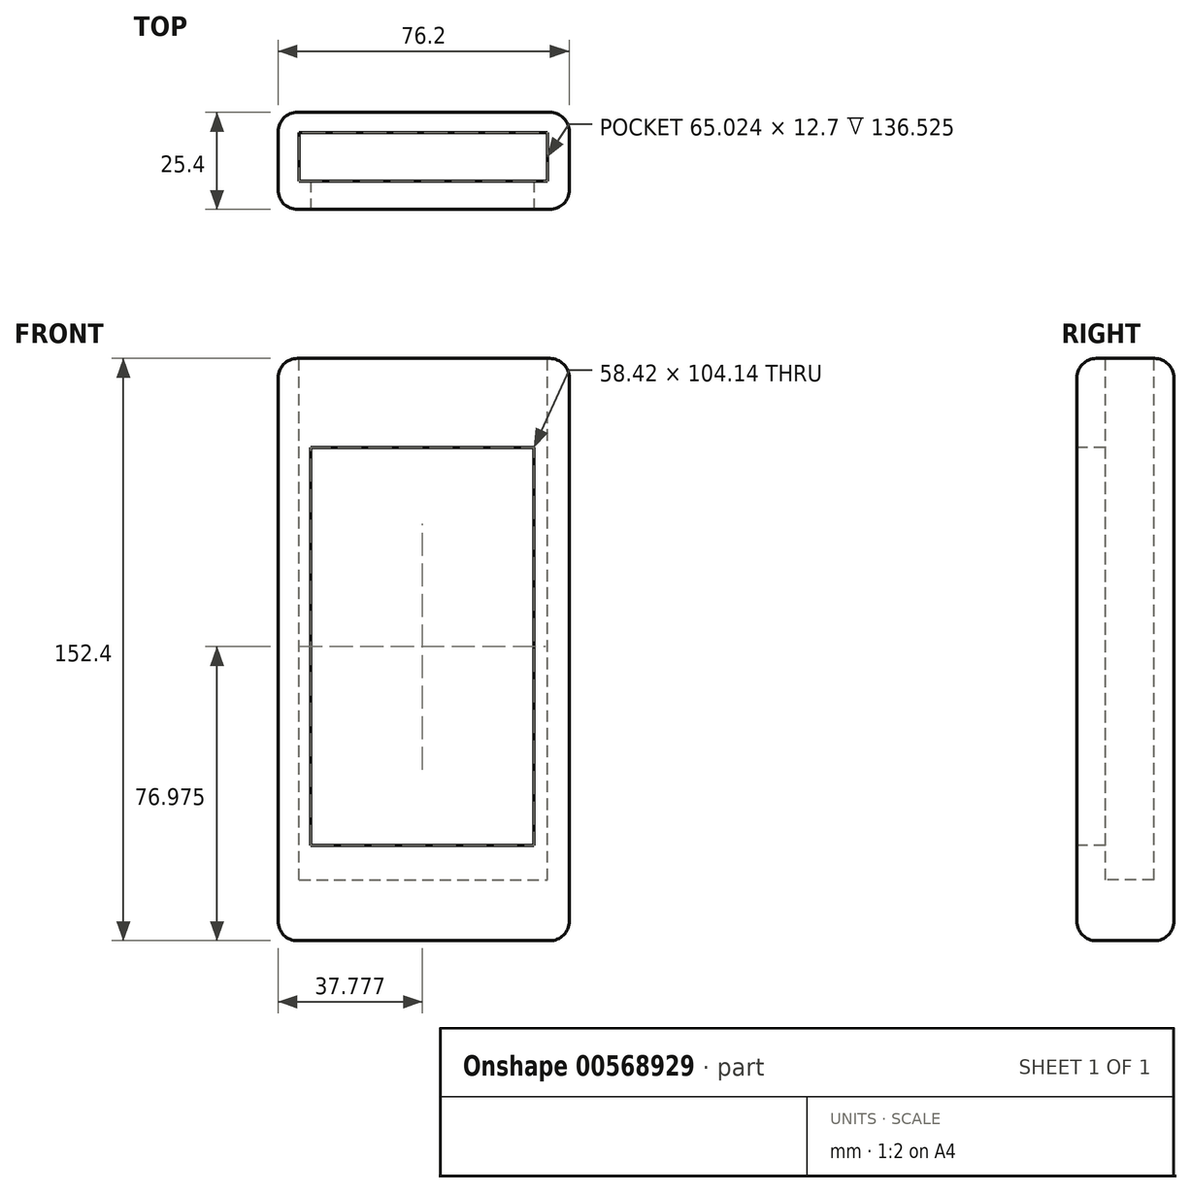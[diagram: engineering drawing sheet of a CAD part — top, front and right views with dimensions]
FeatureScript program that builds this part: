
annotation { "Feature Type Name" : "Feature", "Feature Type Description" : "" }
export const myFeature = defineFeature(function(context is Context, id is Id, definition is map)
    precondition{}
    {
        {
            var Q0;
            Q0=qCreatedBy(makeId("Front.planeOp"),FACE);
            var sketch = newSketch(context, id + "F0", { "sketchPlane" : qUnion([Q0])});
            skLineSegment(sketch, "E0.bottom", {"start": v(-35.38, 75.55) * mm, "end": v(40.82, 75.55) * mm});
            skLineSegment(sketch, "E0.top", {"start": v(-35.38, -76.85) * mm, "end": v(40.82, -76.85) * mm});
            skLineSegment(sketch, "E0.left", {"start": v(-35.38, 75.55) * mm, "end": v(-35.38, -76.85) * mm});
            skLineSegment(sketch, "E0.right", {"start": v(40.82, 75.55) * mm, "end": v(40.82, -76.85) * mm});
            skSolve(sketch);
        }
        {
            var Q0;
            Q0=makeQuery(id+"F0.imprint","IMPRINT",FACE,{"disambiguationData":[TD([[makeQuery(id+"F0.imprint","IMPRINT",EDGE,{"derivedFrom":sQuery(id+"F0.wireOp",EDGE,"E0.bottom")}),-1.0]])]});
            extrude(context, id + "F1", {"entities" : qUnion([Q0]), "depth" : 25.4 * mm, "offsetDistance" : 25.4 * mm});
        }
        {
            var Q0;
            Q0=makeQuery(id+"F1.opExtrude","SWEPT_FACE",FACE,{"disambiguationData":[OSD([sQuery(id+"F0.wireOp",EDGE,"E0.bottom")])]});
            var sketch = newSketch(context, id + "F2", { "sketchPlane" : qUnion([Q0])});
            skLineSegment(sketch, "E1.bottom", {"start": v(-29.89, -5.25) * mm, "end": v(35.14, -5.25) * mm});
            skLineSegment(sketch, "E1.top", {"start": v(-29.89, -17.95) * mm, "end": v(35.14, -17.95) * mm});
            skLineSegment(sketch, "E1.left", {"start": v(-29.89, -5.25) * mm, "end": v(-29.89, -17.95) * mm});
            skLineSegment(sketch, "E1.right", {"start": v(35.14, -5.25) * mm, "end": v(35.14, -17.95) * mm});
            skSolve(sketch);
        }
        {
            var Q0;
            Q0=makeQuery(id+"F2.imprint","IMPRINT",FACE,{"disambiguationData":[TD([[makeQuery(id+"F2.imprint","IMPRINT",EDGE,{"derivedFrom":sQuery(id+"F2.wireOp",EDGE,"E1.bottom")}),-1.0]])]});
            extrude(context, id + "F3", {"entities" : qUnion([Q0]), "operationType" : NewBodyOperationType.REMOVE, "oppositeDirection" : true, "depth" : 136.53 * mm, "offsetDistance" : 25.4 * mm});
        }
        {
            var Q0;
            Q0=makeQuery(id+"F1.opExtrude","CAP_EDGE",EDGE,{"disambiguationData":[OSD([sQuery(id+"F0.wireOp",EDGE,"E0.right")])],"isStart":false});
            var Q1;
            Q1=makeQuery(id+"F1.opExtrude","CAP_EDGE",EDGE,{"disambiguationData":[OSD([sQuery(id+"F0.wireOp",EDGE,"E0.right")])],"isStart":true});
            var Q2;
            Q2=makeQuery(id+"F1.opExtrude","CAP_EDGE",EDGE,{"disambiguationData":[OSD([sQuery(id+"F0.wireOp",EDGE,"E0.left")])],"isStart":true});
            var Q3;
            Q3=makeQuery(id+"F1.opExtrude","CAP_EDGE",EDGE,{"disambiguationData":[OSD([sQuery(id+"F0.wireOp",EDGE,"E0.left")])],"isStart":false});
            var Q4;
            Q4=makeQuery(id+"F1.opExtrude","CAP_EDGE",EDGE,{"disambiguationData":[OSD([sQuery(id+"F0.wireOp",EDGE,"E0.top")])],"isStart":false});
            var Q5;
            Q5=makeQuery(id+"F1.opExtrude","SWEPT_EDGE",EDGE,{"disambiguationData":[OSD([sQuery(id+"F0.wireOp",EDGE,"E0.top"),sQuery(id+"F0.wireOp",EDGE,"E0.left")])]});
            var Q6;
            Q6=makeQuery(id+"F1.opExtrude","SWEPT_EDGE",EDGE,{"disambiguationData":[OSD([sQuery(id+"F0.wireOp",EDGE,"E0.top"),sQuery(id+"F0.wireOp",EDGE,"E0.right")])]});
            var Q7;
            Q7=makeQuery(id+"F1.opExtrude","CAP_EDGE",EDGE,{"disambiguationData":[OSD([sQuery(id+"F0.wireOp",EDGE,"E0.top")])],"isStart":true});
            var Q8;
            Q8=makeQuery(id+"F1.opExtrude","CAP_EDGE",EDGE,{"disambiguationData":[OSD([sQuery(id+"F0.wireOp",EDGE,"E0.bottom")])],"isStart":false});
            var Q9;
            Q9=makeQuery(id+"F1.opExtrude","SWEPT_EDGE",EDGE,{"disambiguationData":[OSD([sQuery(id+"F0.wireOp",EDGE,"E0.bottom"),sQuery(id+"F0.wireOp",EDGE,"E0.left")])]});
            var Q10;
            Q10=makeQuery(id+"F1.opExtrude","SWEPT_EDGE",EDGE,{"disambiguationData":[OSD([sQuery(id+"F0.wireOp",EDGE,"E0.bottom"),sQuery(id+"F0.wireOp",EDGE,"E0.right")])]});
            var Q11;
            Q11=makeQuery(id+"F1.opExtrude","CAP_EDGE",EDGE,{"disambiguationData":[OSD([sQuery(id+"F0.wireOp",EDGE,"E0.bottom")])],"isStart":true});
            fillet(context, id + "F4", {"entities" : qUnion([Q0, Q1, Q2, Q3, Q4, Q5, Q6, Q7, Q8, Q9, Q10, Q11]), "radius" : 5.08 * mm, "tangentPropagation" : true, "allowEdgeOverflow" : false});
        }
        {
            var Q0;
            Q0=makeQuery(id+"F1.opExtrude","CAP_FACE",FACE,{"disambiguationData":[OSD([sQuery(id+"F0.wireOp",EDGE,"E0.bottom"),sQuery(id+"F0.wireOp",EDGE,"E0.top"),sQuery(id+"F0.wireOp",EDGE,"E0.left"),sQuery(id+"F0.wireOp",EDGE,"E0.right")])],"isStart":false});
            var sketch = newSketch(context, id + "F5", { "sketchPlane" : qUnion([Q0])});
            skLineSegment(sketch, "E2", {"start": v(-26.81, 52.2) * mm, "end": v(31.6, 52.2) * mm});
            skLineSegment(sketch, "E3", {"start": v(31.6, 52.2) * mm, "end": v(31.6, -51.94) * mm});
            skLineSegment(sketch, "E4", {"start": v(31.6, -51.94) * mm, "end": v(-26.81, -51.94) * mm});
            skLineSegment(sketch, "E5", {"start": v(-26.81, -51.94) * mm, "end": v(-26.81, 52.2) * mm});
            skSolve(sketch);
        }
        {
            var Q0;
            Q0=makeQuery(id+"F5.imprint","IMPRINT",FACE,{"disambiguationData":[TD([[makeQuery(id+"F5.imprint","IMPRINT",EDGE,{"derivedFrom":sQuery(id+"F5.wireOp",EDGE,"E2")}),-1.0]])]});
            extrude(context, id + "F6", {"entities" : qUnion([Q0]), "operationType" : NewBodyOperationType.REMOVE, "oppositeDirection" : true, "depth" : 7.62 * mm, "offsetDistance" : 25.4 * mm});
        }
    });
